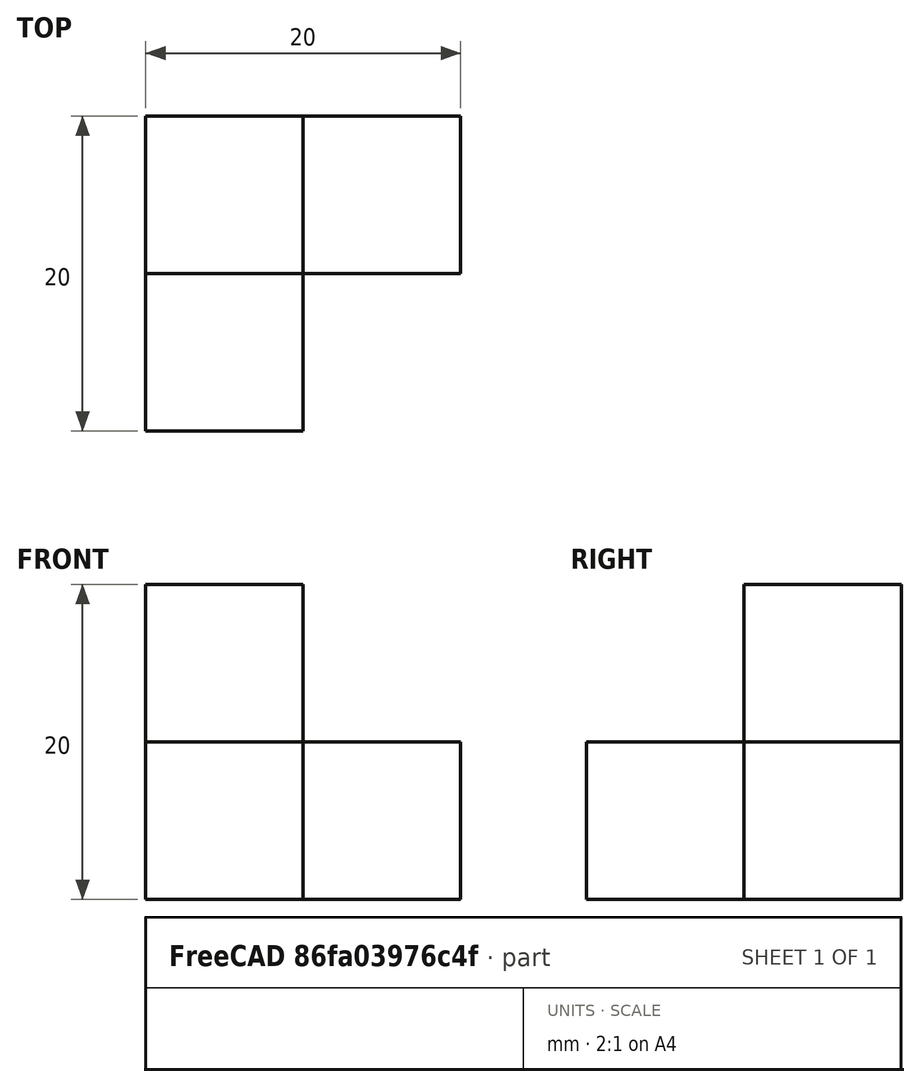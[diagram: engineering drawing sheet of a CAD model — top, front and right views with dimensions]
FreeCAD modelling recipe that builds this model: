
FCSTD DOCUMENT  (FreeCAD 0.21R33694 (Git))
Label: OJT1_T04_P01
License: All rights reserved
LicenseURL: https://en.wikipedia.org/wiki/All_rights_reserved
objects: Part::Box×3, Part::MultiFuse×1, Part::Refine×1
note: 5 computed .brp shape members not serialized (recipe doc carries the construction recipe); baked Part::Feature solids carry a one-line shape summary decoded from their .brp

FEATURE [Part::Box] Box  label="Nivel 1 "
  AttacherType = Attacher::AttachEngine3D
  Height = 20
  Length = 10
  Placement = pos=(0,10,0) rot=(0,0,1;0rad)
  Width = 10
  expr: .Placement.Base.y = 10
  expr: .Placement.Base.z = 0
FEATURE [Part::Box] Box001  label="Nivel 2- cub 1 "
  AttacherType = Attacher::AttachEngine3D
  Height = 10
  Length = 10
  Placement = pos=(10,10,0) rot=(0,0,1;0rad)
  Width = 10
  expr: .Placement.Base.x = 10
  expr: .Placement.Base.y = 10
FEATURE [Part::Box] Box002  label="NIvel 2- cub2 "
  AttacherType = Attacher::AttachEngine3D
  Height = 10
  Length = 10
  Width = 10
FEATURE [Part::MultiFuse] Fusion
  Shapes = -> [Box,Box001,Box002]
FEATURE [Part::Refine] Fusion001
  Source = -> Fusion
